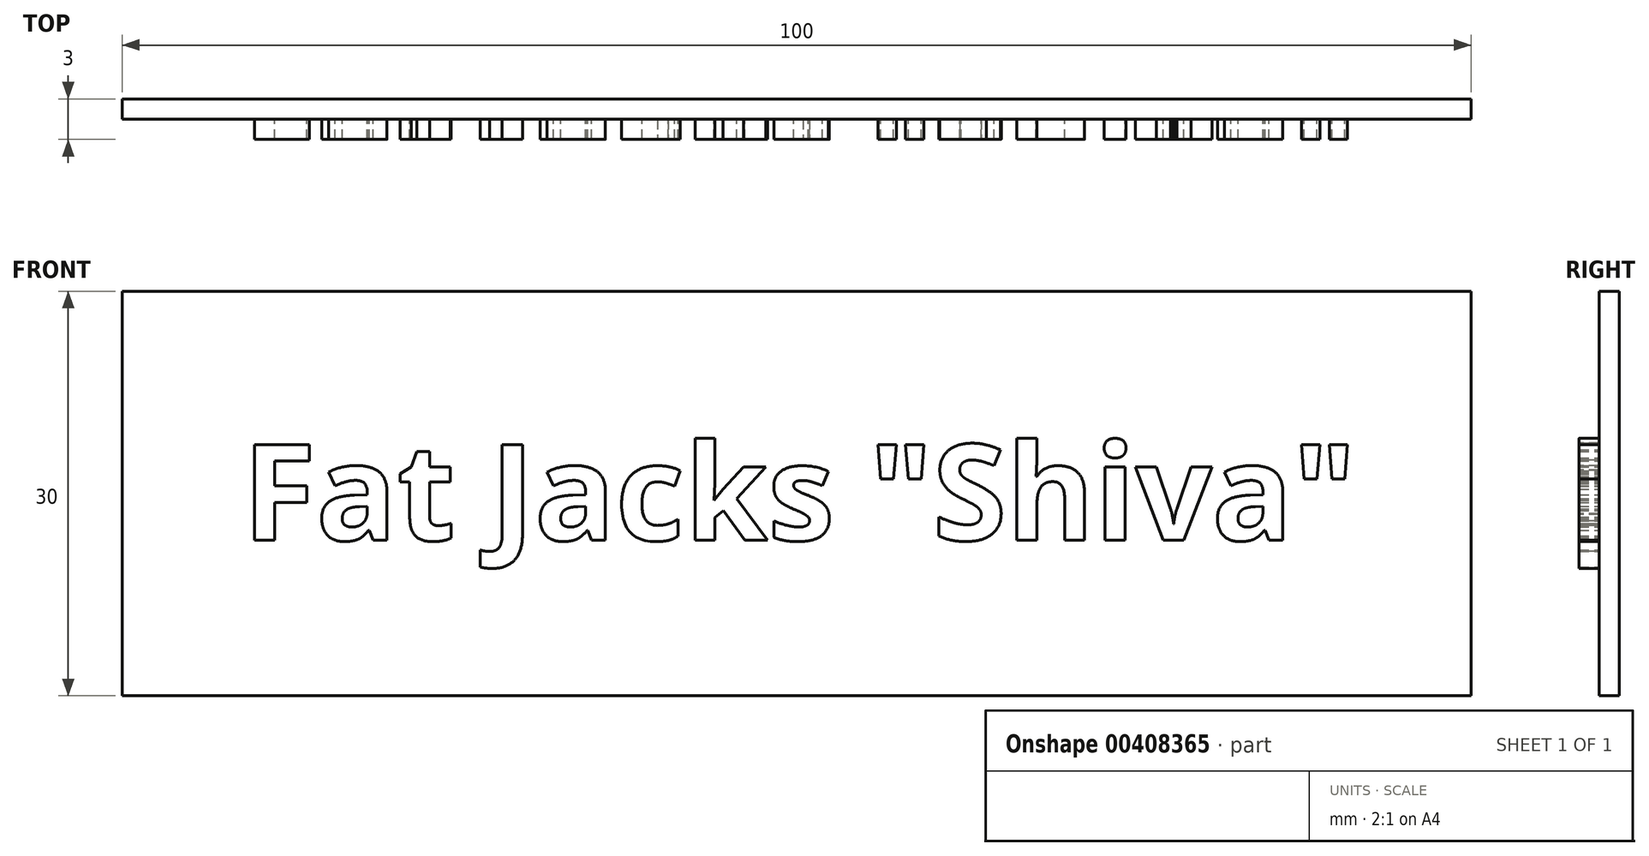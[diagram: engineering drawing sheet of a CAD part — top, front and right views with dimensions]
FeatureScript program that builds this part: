
annotation { "Feature Type Name" : "Feature", "Feature Type Description" : "" }
export const myFeature = defineFeature(function(context is Context, id is Id, definition is map)
    precondition{}
    {
        {
            var Q0;
            Q0=qCreatedBy(makeId("Front.planeOp"),FACE);
            var sketch = newSketch(context, id + "F0", { "sketchPlane" : qUnion([Q0])});
            skLineSegment(sketch, "E0", {"start": v(0, 0) * mm, "end": v(50, 0) * mm});
            skLineSegment(sketch, "E1", {"start": v(50, 0) * mm, "end": v(50, 30) * mm});
            skLineSegment(sketch, "E2", {"start": v(50, 30) * mm, "end": v(0, 30) * mm});
            skLineSegment(sketch, "E3", {"start": v(0, 30) * mm, "end": v(0, 0) * mm});
            skLineSegment(sketch, "E4.MirrorCS", {"start": v(-50, 30) * mm, "end": v(0, 30) * mm});
            skLineSegment(sketch, "E5.MirrorCS", {"start": v(-50, 0) * mm, "end": v(-50, 30) * mm});
            skLineSegment(sketch, "E6.MirrorCS", {"start": v(0, 0) * mm, "end": v(-50, 0) * mm});
            skSolve(sketch);
        }
        {
            var Q0;
            Q0=makeQuery(id+"F0.imprint","IMPRINT",FACE,{"disambiguationData":[TD([[makeQuery(id+"F0.imprint","IMPRINT",EDGE,{"derivedFrom":sQuery(id+"F0.wireOp",EDGE,"E0")}),1.0]])]});
            var Q1;
            Q1=makeQuery(id+"F0.imprint","IMPRINT",FACE,{"disambiguationData":[TD([[makeQuery(id+"F0.imprint","IMPRINT",EDGE,{"derivedFrom":sQuery(id+"F0.wireOp",EDGE,"E3")}),-1.0]])]});
            extrude(context, id + "F1", {"entities" : qUnion([Q0, Q1]), "depth" : 1.5 * mm});
        }
        {
            var Q0;
            Q0=makeQuery(id+"F1.opExtrude","CAP_FACE",FACE,{"disambiguationData":[OSD([sQuery(id+"F0.wireOp",EDGE,"E0"),sQuery(id+"F0.wireOp",EDGE,"E1"),sQuery(id+"F0.wireOp",EDGE,"E2"),sQuery(id+"F0.wireOp",EDGE,"E4.MirrorCS"),sQuery(id+"F0.wireOp",EDGE,"E5.MirrorCS"),sQuery(id+"F0.wireOp",EDGE,"E6.MirrorCS")])],"isStart":false});
            var sketch = newSketch(context, id + "F2", { "sketchPlane" : qUnion([Q0])});
            skText(sketch, "E7", { "text": "Fat Jacks \"Shiva\"", "fontName": "OpenSans-Bold.ttf"});
            const initialGuessF2  = {"E7": [-0.04109, 0.01153, 1, 0, 0.00716]};
            skSetInitialGuess(sketch, initialGuessF2);
            skSolve(sketch);
        }
        {
            var Q0;
            Q0=qSketchRegion(id+"F2",true);
            extrude(context, id + "F3", {"entities" : qUnion([Q0]), "operationType" : NewBodyOperationType.ADD, "depth" : 1.5 * mm});
        }
    });
